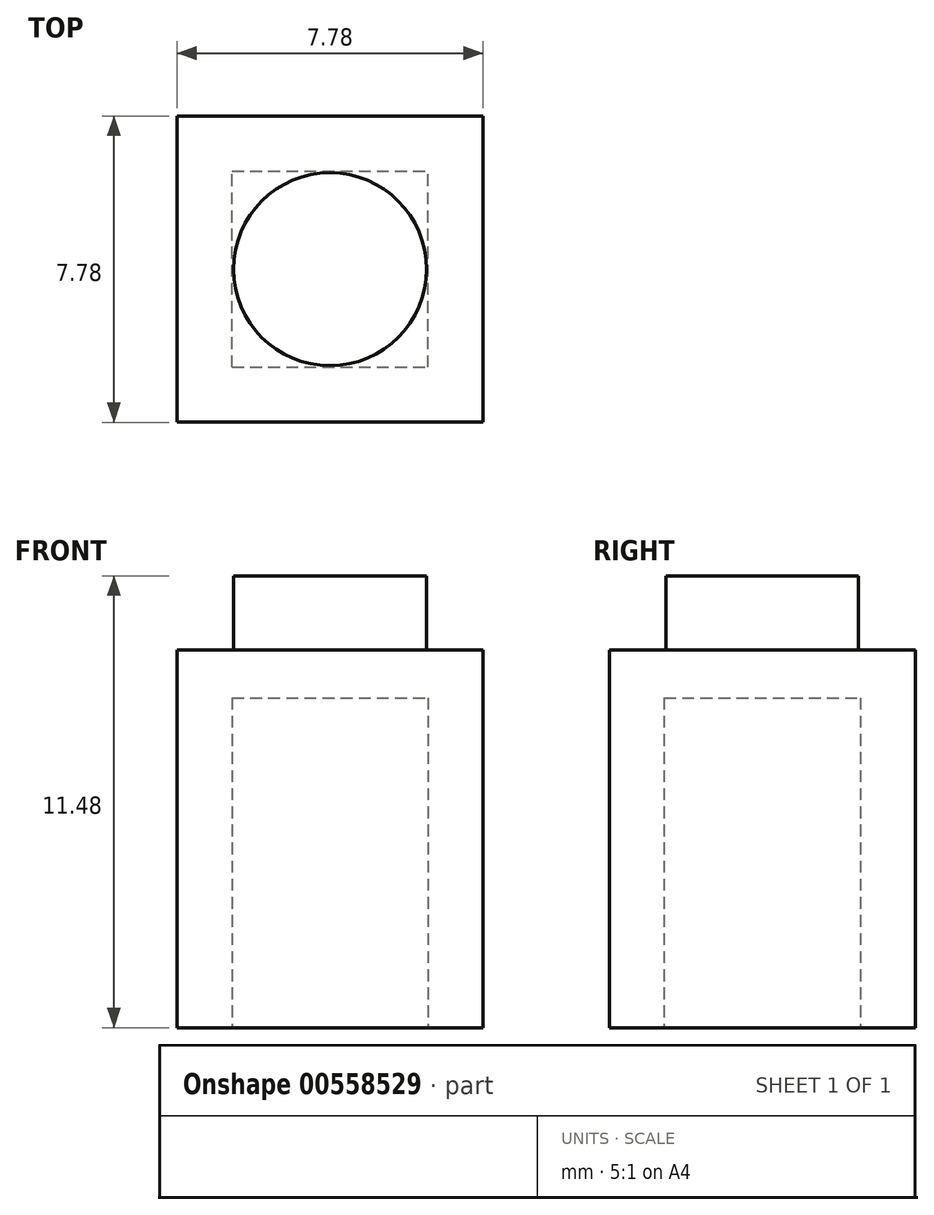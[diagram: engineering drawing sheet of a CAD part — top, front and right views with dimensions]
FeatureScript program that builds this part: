
annotation { "Feature Type Name" : "Feature", "Feature Type Description" : "" }
export const myFeature = defineFeature(function(context is Context, id is Id, definition is map)
    precondition{}
    {
        {
            var Q0;
            Q0=qCreatedBy(makeId("Top.planeOp"),FACE);
            var sketch = newSketch(context, id + "F0", { "sketchPlane" : qUnion([Q0])});
            skLineSegment(sketch, "E0.bottom", {"start": v(-3.89, 3.89) * mm, "end": v(3.89, 3.89) * mm});
            skLineSegment(sketch, "E0.top", {"start": v(-3.89, -3.89) * mm, "end": v(3.89, -3.89) * mm});
            skLineSegment(sketch, "E0.left", {"start": v(-3.89, 3.89) * mm, "end": v(-3.89, -3.89) * mm});
            skLineSegment(sketch, "E0.right", {"start": v(3.89, 3.89) * mm, "end": v(3.89, -3.89) * mm});
            skPoint(sketch, "E0.middle", {"position": v(0, 0) * mm});
            skSolve(sketch);
        }
        {
            var Q0;
            Q0 = qSketchRegion(id + "F0", true);
            extrude(context, id + "F1", {"entities" : qUnion([Q0]), "depth" : 9.6 * mm, "offsetDistance" : 25.4 * mm});
        }
        {
            var Q0;
            Q0=makeQuery(id+"F1.opExtrude","CAP_FACE",FACE,{"disambiguationData":[OSD([sQuery(id+"F0.wireOp",EDGE,"E0.bottom"),sQuery(id+"F0.wireOp",EDGE,"E0.top"),sQuery(id+"F0.wireOp",EDGE,"E0.left"),sQuery(id+"F0.wireOp",EDGE,"E0.right")])],"isStart":false});
            var sketch = newSketch(context, id + "F2", { "sketchPlane" : qUnion([Q0])});
            skCircle(sketch, "E1", {"center": v(0, 0) * mm, "radius": 2.45 * mm});
            skSolve(sketch);
        }
        {
            var Q0;
            Q0=makeQuery(id+"F2.imprint","IMPRINT",FACE,{"disambiguationData":[TD([[makeQuery(id+"F2.imprint","IMPRINT",EDGE,{"derivedFrom":sQuery(id+"F2.wireOp",EDGE,"E1")}),1.0]])]});
            extrude(context, id + "F3", {"entities" : qUnion([Q0]), "operationType" : NewBodyOperationType.ADD, "depth" : 1.88 * mm, "offsetDistance" : 25.4 * mm});
        }
        {
            var Q0;
            Q0=makeQuery(id+"F1.opExtrude","CAP_FACE",FACE,{"disambiguationData":[OSD([sQuery(id+"F0.wireOp",EDGE,"E0.bottom"),sQuery(id+"F0.wireOp",EDGE,"E0.top"),sQuery(id+"F0.wireOp",EDGE,"E0.left"),sQuery(id+"F0.wireOp",EDGE,"E0.right")])],"isStart":true});
            var sketch = newSketch(context, id + "F4", { "sketchPlane" : qUnion([Q0])});
            skLineSegment(sketch, "E2.bottom", {"start": v(-2.49, 2.49) * mm, "end": v(2.49, 2.49) * mm});
            skLineSegment(sketch, "E2.top", {"start": v(-2.49, -2.49) * mm, "end": v(2.49, -2.49) * mm});
            skLineSegment(sketch, "E2.left", {"start": v(-2.49, 2.49) * mm, "end": v(-2.49, -2.49) * mm});
            skLineSegment(sketch, "E2.right", {"start": v(2.49, 2.49) * mm, "end": v(2.49, -2.49) * mm});
            skPoint(sketch, "E2.middle", {"position": v(0, 0) * mm});
            skSolve(sketch);
        }
        {
            var Q0;
            Q0=makeQuery(id+"F4.imprint","IMPRINT",FACE,{"disambiguationData":[TD([[makeQuery(id+"F4.imprint","IMPRINT",EDGE,{"derivedFrom":sQuery(id+"F4.wireOp",EDGE,"E2.bottom")}),-1.0]])]});
            extrude(context, id + "F5", {"entities" : qUnion([Q0]), "operationType" : NewBodyOperationType.REMOVE, "oppositeDirection" : true, "depth" : 8.38 * mm, "offsetDistance" : 25.4 * mm});
        }
    });
